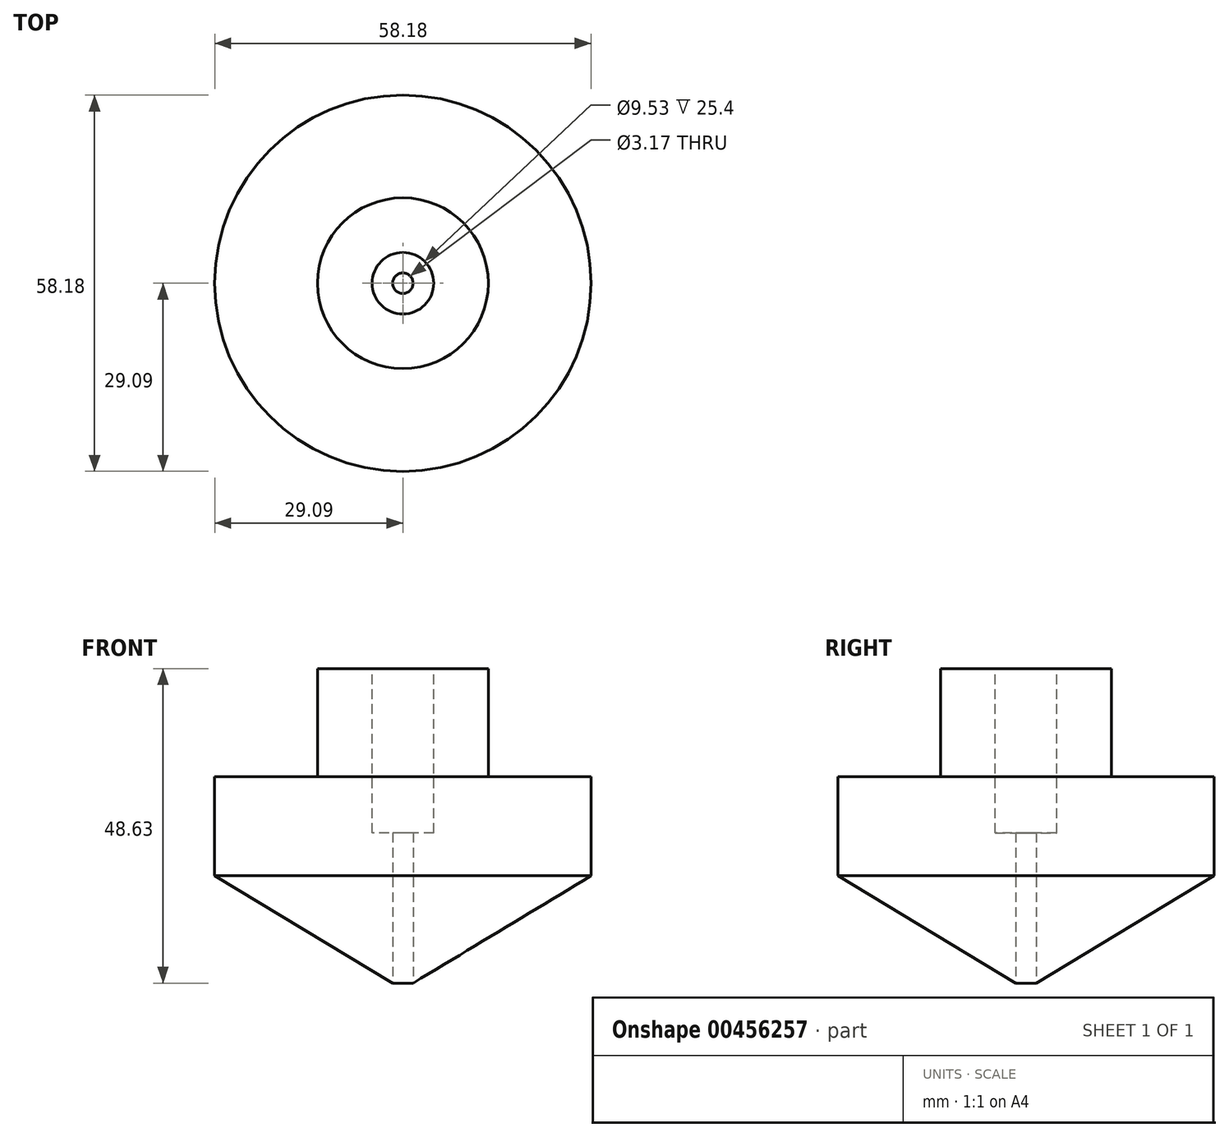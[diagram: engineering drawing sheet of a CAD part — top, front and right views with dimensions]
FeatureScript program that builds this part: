
annotation { "Feature Type Name" : "Feature", "Feature Type Description" : "" }
export const myFeature = defineFeature(function(context is Context, id is Id, definition is map)
    precondition{}
    {
        {
            var Q0;
            Q0=qCreatedBy(makeId("Front.planeOp"),FACE);
            var sketch = newSketch(context, id + "F0", { "sketchPlane" : qUnion([Q0])});
            skLineSegment(sketch, "E0", {"start": v(0, 0) * mm, "end": v(29.1, 17.54) * mm});
            skLineSegment(sketch, "E1", {"start": v(29.1, 17.54) * mm, "end": v(29.1, 32.85) * mm});
            skLineSegment(sketch, "E2", {"start": v(29.1, 32.85) * mm, "end": v(13.2, 32.85) * mm});
            skLineSegment(sketch, "E3", {"start": v(13.2, 32.85) * mm, "end": v(13.2, 49.6) * mm});
            skLineSegment(sketch, "E4", {"start": v(13.2, 49.6) * mm, "end": v(0, 49.6) * mm});
            skLineSegment(sketch, "E5", {"start": v(0, 0) * mm, "end": v(0, 49.6) * mm});
            skSolve(sketch);
        }
        {
            var Q0;
            Q0 = qSketchRegion(id + "F0", true);
            var Q1;
            Q1=sQuery(id+"F0.wireOp",EDGE,"E5");
            revolve(context, id + "F1", {"entities" : qUnion([Q0]), "axis" : qUnion([Q1]), "revolveType" : RevolveType.FULL});
        }
        {
            var Q0;
            Q0=makeQuery(id+"F1.opRevolve","SWEPT_FACE",FACE,{"disambiguationData":[OSD([sQuery(id+"F0.wireOp",EDGE,"E4")])]});
            var sketch = newSketch(context, id + "F2", { "sketchPlane" : qUnion([Q0])});
            skCircle(sketch, "E6", {"center": v(0, 0) * mm, "radius": 4.76 * mm});
            skSolve(sketch);
        }
        {
            var Q0;
            Q0=makeQuery(id+"F2.imprint","IMPRINT",FACE,{"disambiguationData":[TD([[makeQuery(id+"F2.imprint","IMPRINT",EDGE,{"derivedFrom":sQuery(id+"F2.wireOp",EDGE,"E6")}),1.0]])]});
            var sketch = newSketch(context, id + "F3", { "sketchPlane" : qUnion([Q0])});
            skSolve(sketch);
        }
        {
            var Q0;
            Q0 = qSketchRegion(id + "F3", true);
            var Q1;
            Q1=makeQuery(id+"F2.imprint","IMPRINT",FACE,{"disambiguationData":[TD([[makeQuery(id+"F2.imprint","IMPRINT",EDGE,{"derivedFrom":sQuery(id+"F2.wireOp",EDGE,"E6")}),1.0]])]});
            extrude(context, id + "F4", {"entities" : qUnion([Q0, Q1]), "operationType" : NewBodyOperationType.REMOVE, "oppositeDirection" : true, "depth" : 25.4 * mm});
        }
        {
            var Q0;
            Q0=qCreatedBy(makeId("Top.planeOp"),FACE);
            var sketch = newSketch(context, id + "F5", { "sketchPlane" : qUnion([Q0])});
            skCircle(sketch, "E7", {"center": v(0, 0) * mm, "radius": 1.6 * mm});
            skCircle(sketch, "E8", {"center": v(0, 0) * mm, "radius": 1.59 * mm});
            skSolve(sketch);
        }
        {
            var Q0;
            Q0=makeQuery(id+"F5.imprint","IMPRINT",FACE,{"disambiguationData":[TD([[makeQuery(id+"F5.imprint","IMPRINT",EDGE,{"derivedFrom":sQuery(id+"F5.wireOp",EDGE,"E8")}),1.0]])]});
            extrude(context, id + "F6", {"entities" : qUnion([Q0]), "operationType" : NewBodyOperationType.REMOVE, "depth" : 25.4 * mm});
        }
    });
